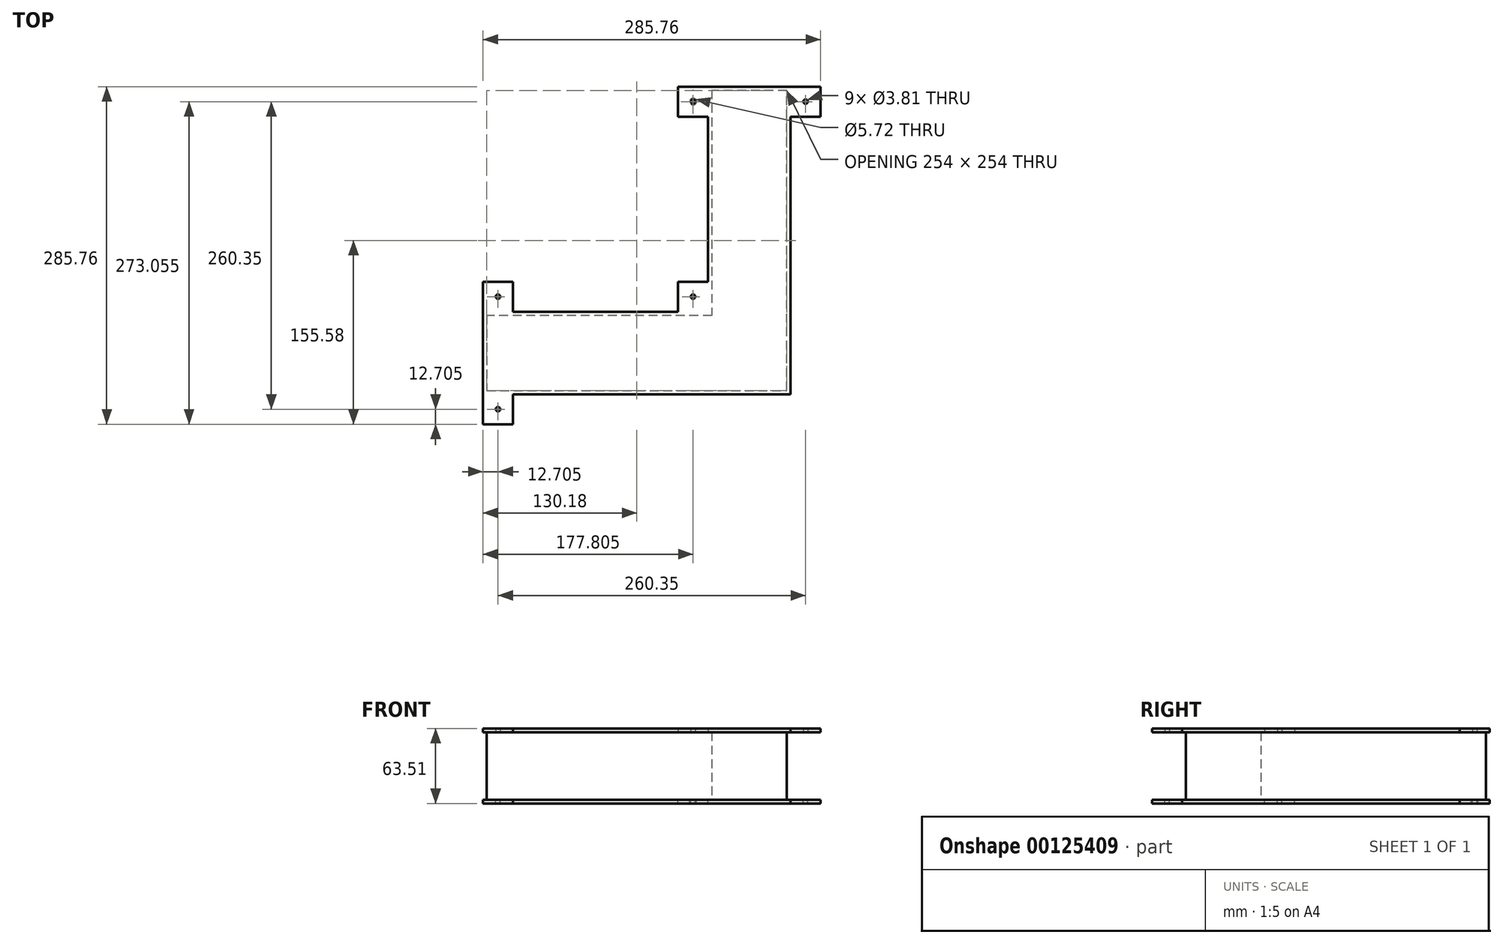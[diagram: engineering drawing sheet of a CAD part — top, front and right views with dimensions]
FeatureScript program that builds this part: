
annotation { "Feature Type Name" : "Feature", "Feature Type Description" : "" }
export const myFeature = defineFeature(function(context is Context, id is Id, definition is map)
    precondition{}
    {
        {
            var Q0;
            Q0=qCreatedBy(makeId("Top.planeOp"),FACE);
            var sketch = newSketch(context, id + "F0", { "sketchPlane" : qUnion([Q0])});
            skLineSegment(sketch, "E0", {"start": v(-190.5, -63.5) * mm, "end": v(63.5, -63.5) * mm});
            skLineSegment(sketch, "E1", {"start": v(63.5, -63.5) * mm, "end": v(63.5, 190.5) * mm});
            skLineSegment(sketch, "E2", {"start": v(63.5, 190.5) * mm, "end": v(0, 190.5) * mm});
            skLineSegment(sketch, "E3", {"start": v(0, 190.5) * mm, "end": v(0, 0) * mm});
            skLineSegment(sketch, "E4", {"start": v(0, 0) * mm, "end": v(-190.5, 0) * mm});
            skLineSegment(sketch, "E5", {"start": v(-190.5, 0) * mm, "end": v(-190.5, -63.5) * mm});
            skSolve(sketch);
        }
        {
            var Q0;
            Q0=makeQuery(id+"F0.imprint","IMPRINT",FACE,{"disambiguationData":[TD([[makeQuery(id+"F0.imprint","IMPRINT",EDGE,{"derivedFrom":sQuery(id+"F0.wireOp",EDGE,"E0")}),1.0]])]});
            extrude(context, id + "F1", {"entities" : qUnion([Q0]), "depth" : 57.15 * mm});
        }
        {
            var Q0;
            Q0=makeQuery(id+"F1.opExtrude","CAP_FACE",FACE,{"disambiguationData":[OSD([sQuery(id+"F0.wireOp",EDGE,"E0"),sQuery(id+"F0.wireOp",EDGE,"E2"),sQuery(id+"F0.wireOp",EDGE,"E3"),sQuery(id+"F0.wireOp",EDGE,"E4"),sQuery(id+"F0.wireOp",EDGE,"E5"),sQuery(id+"F0.wireOp",EDGE,"E1")])],"isStart":true});
            var sketch = newSketch(context, id + "F2", { "sketchPlane" : qUnion([Q0])});
            skLineSegment(sketch, "E6", {"start": v(-28.57, -3.17) * mm, "end": v(-168.28, -3.17) * mm});
            skLineSegment(sketch, "E7", {"start": v(-193.68, -3.17) * mm, "end": v(-193.68, 66.68) * mm});
            skLineSegment(sketch, "E8", {"start": v(-168.28, 66.68) * mm, "end": v(66.67, 66.68) * mm});
            skLineSegment(sketch, "E9", {"start": v(66.67, 66.68) * mm, "end": v(66.67, -168.28) * mm});
            skLineSegment(sketch, "E10", {"start": v(66.67, -193.68) * mm, "end": v(-3.18, -193.68) * mm});
            skLineSegment(sketch, "E11", {"start": v(-3.18, -168.28) * mm, "end": v(-3.17, -28.58) * mm});
            skLineSegment(sketch, "E12", {"start": v(-193.68, -3.17) * mm, "end": v(-193.68, -28.57) * mm});
            skLineSegment(sketch, "E13", {"start": v(-193.68, -28.57) * mm, "end": v(-168.28, -28.57) * mm});
            skLineSegment(sketch, "E14", {"start": v(-168.28, -28.57) * mm, "end": v(-168.28, -3.17) * mm});
            skLineSegment(sketch, "E15", {"start": v(-193.68, 66.68) * mm, "end": v(-193.68, 92.08) * mm});
            skLineSegment(sketch, "E16", {"start": v(-193.68, 92.08) * mm, "end": v(-168.28, 92.08) * mm});
            skLineSegment(sketch, "E17", {"start": v(-168.28, 92.08) * mm, "end": v(-168.28, 66.68) * mm});
            skLineSegment(sketch, "E18", {"start": v(-3.18, -193.68) * mm, "end": v(-28.58, -193.68) * mm});
            skLineSegment(sketch, "E19", {"start": v(-28.58, -193.68) * mm, "end": v(-28.58, -168.28) * mm});
            skLineSegment(sketch, "E20", {"start": v(-28.58, -168.28) * mm, "end": v(-3.18, -168.28) * mm});
            skLineSegment(sketch, "E21", {"start": v(66.67, -193.68) * mm, "end": v(92.08, -193.68) * mm});
            skLineSegment(sketch, "E22", {"start": v(92.08, -193.68) * mm, "end": v(92.08, -168.28) * mm});
            skLineSegment(sketch, "E23", {"start": v(92.08, -168.28) * mm, "end": v(66.67, -168.28) * mm});
            skLineSegment(sketch, "E24", {"start": v(-3.17, -28.58) * mm, "end": v(-28.57, -28.58) * mm});
            skLineSegment(sketch, "E25", {"start": v(-28.57, -28.57) * mm, "end": v(-28.57, -3.17) * mm});
            skCircle(sketch, "E26", {"center": v(-15.87, -15.88) * mm, "radius": 1.9 * mm});
            skCircle(sketch, "E27", {"center": v(-180.98, -15.87) * mm, "radius": 1.9 * mm});
            skCircle(sketch, "E28", {"center": v(-180.97, 79.38) * mm, "radius": 1.9 * mm});
            skPoint(sketch, "E28.centerSnap0", {"position": v(-180.97, 92.08) * mm});
            skCircle(sketch, "E29", {"center": v(-15.88, -180.97) * mm, "radius": 2.86 * mm});
            skPoint(sketch, "E29.centerSnap0", {"position": v(-28.58, -180.97) * mm});
            skCircle(sketch, "E30", {"center": v(79.38, -180.97) * mm, "radius": 1.9 * mm});
            skSolve(sketch);
        }
        {
            var Q0;
            Q0=makeQuery(id+"F2.imprint","IMPRINT",FACE,{"disambiguationData":[TD([[makeQuery(id+"F2.imprint","IMPRINT",EDGE,{"derivedFrom":sQuery(id+"F2.wireOp",EDGE,"E6")}),-1.0]])]});
            var Q1;
            Q1=makeQuery(id+"F2.imprint","IMPRINT",FACE,{"disambiguationData":[TD([[makeQuery(id+"F2.imprint","IMPRINT",EDGE,{"derivedFrom":makeQuery(id+"F1.opExtrude","CAP_EDGE",EDGE,{"disambiguationData":[OSD([sQuery(id+"F0.wireOp",EDGE,"E0")])],"isStart":true})}),-1.0]])]});
            extrude(context, id + "F3", {"entities" : qUnion([Q0, Q1]), "operationType" : NewBodyOperationType.ADD, "depth" : 3.17 * mm});
        }
        {
            var Q0;
            Q0=makeQuery(id+"F1.opExtrude","CAP_FACE",FACE,{"disambiguationData":[OSD([sQuery(id+"F0.wireOp",EDGE,"E0"),sQuery(id+"F0.wireOp",EDGE,"E2"),sQuery(id+"F0.wireOp",EDGE,"E3"),sQuery(id+"F0.wireOp",EDGE,"E4"),sQuery(id+"F0.wireOp",EDGE,"E5"),sQuery(id+"F0.wireOp",EDGE,"E1")])],"isStart":false});
            var sketch = newSketch(context, id + "F4", { "sketchPlane" : qUnion([Q0])});
            skLineSegment(sketch, "E31", {"start": v(-3.18, 168.27) * mm, "end": v(-3.17, 28.58) * mm});
            skLineSegment(sketch, "E32", {"start": v(-28.57, 3.17) * mm, "end": v(-168.28, 3.17) * mm});
            skLineSegment(sketch, "E33", {"start": v(-193.68, 3.17) * mm, "end": v(-193.68, -66.68) * mm});
            skLineSegment(sketch, "E34", {"start": v(-168.27, -66.68) * mm, "end": v(66.67, -66.68) * mm});
            skLineSegment(sketch, "E35", {"start": v(66.68, -66.68) * mm, "end": v(66.67, 168.28) * mm});
            skLineSegment(sketch, "E36", {"start": v(66.67, 193.68) * mm, "end": v(-3.18, 193.68) * mm});
            skLineSegment(sketch, "E37", {"start": v(-193.68, 3.17) * mm, "end": v(-193.68, 28.57) * mm});
            skLineSegment(sketch, "E38", {"start": v(-193.68, 28.57) * mm, "end": v(-168.28, 28.57) * mm});
            skLineSegment(sketch, "E39", {"start": v(-168.28, 28.57) * mm, "end": v(-168.28, 3.17) * mm});
            skLineSegment(sketch, "E40", {"start": v(-193.67, -66.68) * mm, "end": v(-193.67, -92.08) * mm});
            skLineSegment(sketch, "E41", {"start": v(-193.67, -92.08) * mm, "end": v(-168.27, -92.08) * mm});
            skLineSegment(sketch, "E42", {"start": v(-168.27, -92.08) * mm, "end": v(-168.27, -66.68) * mm});
            skLineSegment(sketch, "E43", {"start": v(-3.18, 193.67) * mm, "end": v(-28.58, 193.67) * mm});
            skLineSegment(sketch, "E44", {"start": v(-28.58, 193.67) * mm, "end": v(-28.58, 168.27) * mm});
            skLineSegment(sketch, "E45", {"start": v(-28.58, 168.27) * mm, "end": v(-3.18, 168.27) * mm});
            skLineSegment(sketch, "E46", {"start": v(66.67, 193.68) * mm, "end": v(92.08, 193.68) * mm});
            skLineSegment(sketch, "E47", {"start": v(92.08, 193.68) * mm, "end": v(92.08, 168.28) * mm});
            skLineSegment(sketch, "E48", {"start": v(92.08, 168.28) * mm, "end": v(66.67, 168.28) * mm});
            skLineSegment(sketch, "E49", {"start": v(-28.57, 3.17) * mm, "end": v(-28.57, 28.58) * mm});
            skLineSegment(sketch, "E50", {"start": v(-28.57, 28.58) * mm, "end": v(-3.17, 28.58) * mm});
            skPoint(sketch, "E51.orphan", {"position": v(0, 28.58) * mm});
            skCircle(sketch, "E52", {"center": v(-15.88, 180.97) * mm, "radius": 1.9 * mm});
            skCircle(sketch, "E53", {"center": v(79.38, 180.98) * mm, "radius": 1.9 * mm});
            skCircle(sketch, "E54", {"center": v(-15.87, 15.88) * mm, "radius": 1.9 * mm});
            skCircle(sketch, "E55", {"center": v(-180.97, 15.87) * mm, "radius": 1.9 * mm});
            skCircle(sketch, "E56", {"center": v(-180.97, -79.38) * mm, "radius": 1.9 * mm});
            skSolve(sketch);
        }
        {
            var Q0;
            Q0=qSketchRegion(id+"F4",true);
            extrude(context, id + "F5", {"entities" : qUnion([Q0]), "operationType" : NewBodyOperationType.ADD, "depth" : 3.17 * mm});
        }
    });
